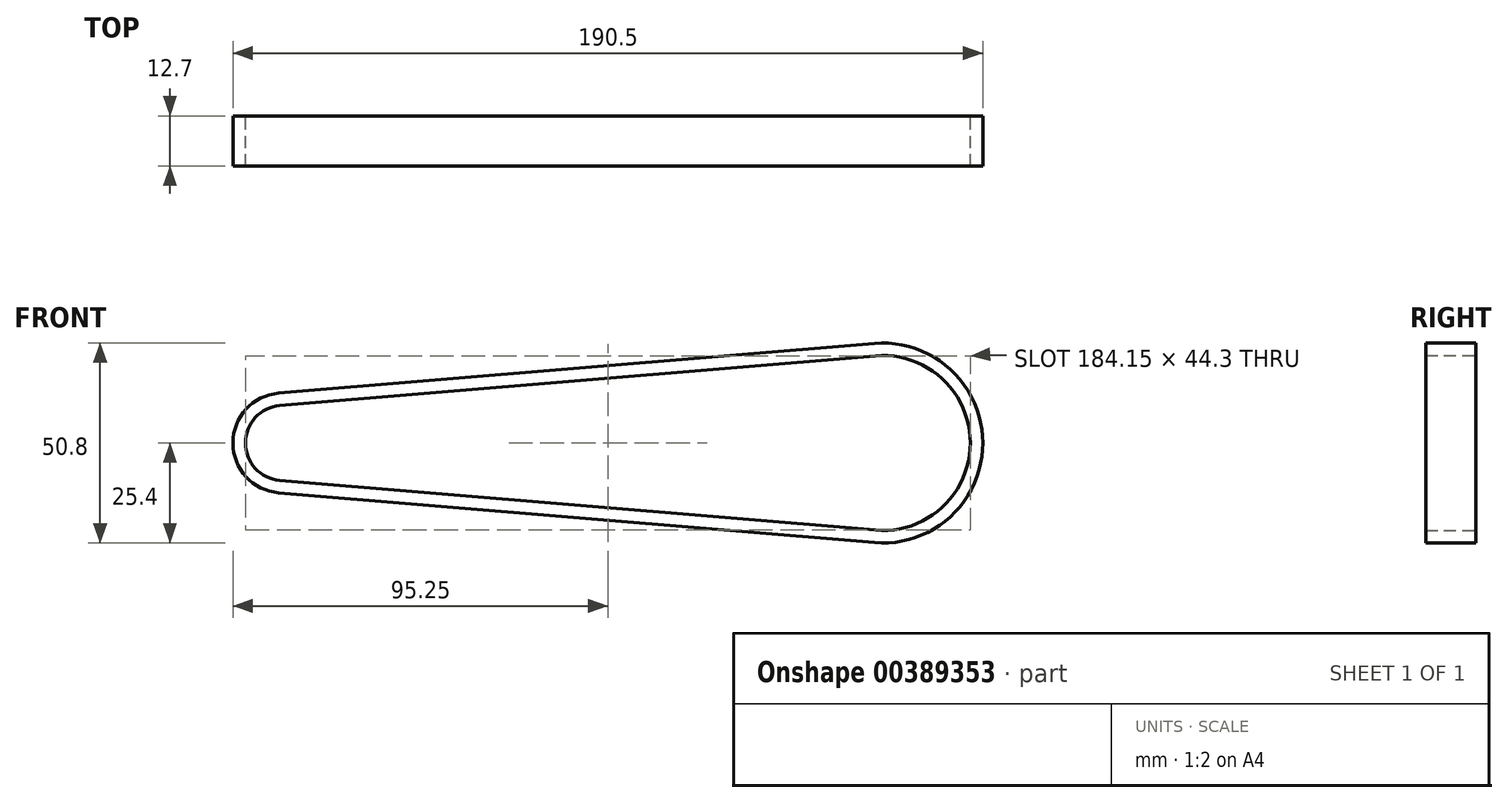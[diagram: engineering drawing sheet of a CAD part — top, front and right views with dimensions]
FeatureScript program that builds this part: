
annotation { "Feature Type Name" : "Feature", "Feature Type Description" : "" }
export const myFeature = defineFeature(function(context is Context, id is Id, definition is map)
    precondition{}
    {
        {
            var Q0;
            Q0=qCreatedBy(makeId("Front.planeOp"),FACE);
            var sketch = newSketch(context, id + "F0", { "sketchPlane" : qUnion([Q0])});
            skArc(sketch, "E0", {"start": v(-1.06, 12.66) * mm, "mid": v(-12.7, 0) * mm, "end": v(-1.06, -12.66) * mm});
            skArc(sketch, "E1", {"start": v(150.28, -25.31) * mm, "mid": v(177.8, 0) * mm, "end": v(150.28, 25.31) * mm});
            skArc(sketch, "E2", {"start": v(-0.8, 9.5) * mm, "mid": v(-9.53, 0) * mm, "end": v(-0.8, -9.5) * mm});
            skCircle(sketch, "E3", {"center": v(152.4, 0) * mm, "radius": 22.23 * mm});
            skLineSegment(sketch, "E4", {"start": v(-1.06, 12.66) * mm, "end": v(150.28, 25.31) * mm});
            skLineSegment(sketch, "E5", {"start": v(-1.06, -12.66) * mm, "end": v(150.28, -25.31) * mm});
            skLineSegment(sketch, "E6", {"start": v(-0.8, -9.5) * mm, "end": v(150.55, -22.15) * mm});
            skLineSegment(sketch, "E7.trimOffspring", {"start": v(-0.8, 9.5) * mm, "end": v(150.55, 22.15) * mm});
            skSolve(sketch);
        }
        {
            var Q0;
            Q0=makeQuery(id+"F0.imprint","IMPRINT",FACE,{"disambiguationData":[TD([[makeQuery(id+"F0.imprint","IMPRINT",EDGE,{"derivedFrom":sQuery(id+"F0.wireOp",EDGE,"E0")}),1.0]])]});
            extrude(context, id + "F1", {"entities" : qUnion([Q0]), "depth" : 12.7 * mm});
        }
    });
